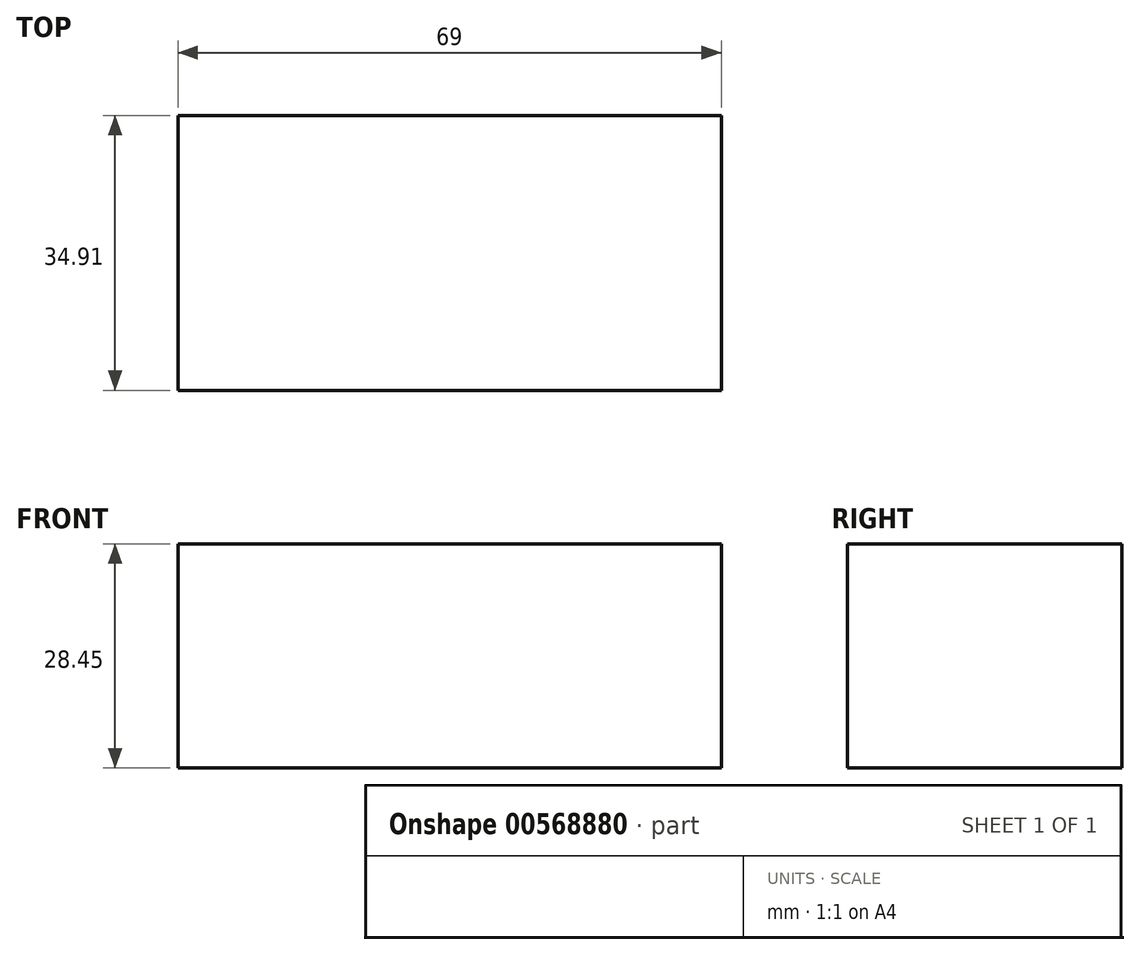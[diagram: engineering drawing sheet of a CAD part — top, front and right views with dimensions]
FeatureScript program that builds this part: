
annotation { "Feature Type Name" : "Feature", "Feature Type Description" : "" }
export const myFeature = defineFeature(function(context is Context, id is Id, definition is map)
    precondition{}
    {
        {
            var Q0;
            Q0=qCreatedBy(makeId("Top.planeOp"),FACE);
            var sketch = newSketch(context, id + "F0", { "sketchPlane" : qUnion([Q0])});
            skLineSegment(sketch, "E0.bottom", {"start": v(-40.81, 42.96) * mm, "end": v(28.2, 42.96) * mm});
            skLineSegment(sketch, "E0.top", {"start": v(-40.81, 8.05) * mm, "end": v(28.2, 8.05) * mm});
            skLineSegment(sketch, "E0.left", {"start": v(-40.81, 42.96) * mm, "end": v(-40.81, 8.05) * mm});
            skLineSegment(sketch, "E0.right", {"start": v(28.2, 42.96) * mm, "end": v(28.2, 8.05) * mm});
            skSolve(sketch);
        }
        {
            var Q0;
            Q0=makeQuery(id+"F0.imprint","IMPRINT",FACE,{"disambiguationData":[TD([[makeQuery(id+"F0.imprint","IMPRINT",EDGE,{"derivedFrom":sQuery(id+"F0.wireOp",EDGE,"E0.bottom")}),-1.0]])]});
            var Q1;
            Q1 = qSketchRegion(id + "F2VxV5LITGYnwXS_0", true);
            extrude(context, id + "F1", {"entities" : qUnion([Q0, Q1]), "depth" : 50.8 * mm, "offsetDistance" : 25.4 * mm, "hasSecondDirection" : true, "secondDirectionOppositeDirection" : false, "secondDirectionDepth" : 22.35 * mm});
        }
    });
